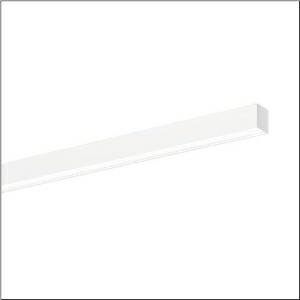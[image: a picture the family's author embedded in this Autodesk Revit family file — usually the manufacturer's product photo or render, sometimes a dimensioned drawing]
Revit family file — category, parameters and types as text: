
# Revit family: silica_21_51mx23dc3awb
name_source: partatom
category: Lighting Fixtures
units: mm (PartAtom-declared; Revit-internal decimal feet)

## family parameters
Cut with Voids When Loaded = No
Host = Face
Light Source = No
Part Type = Normal
Room Calculation Point = No
Round Connector Dimension = Use Diameter
Shared = No

## types (1)
- --- (1 x LED, 8200 lm, 62.2 W, 3000K)
    Apparent Load = 62 VA
    CIE Flux Codes = 78 96 99 100 100
    Color Rendering = 80
    Color Temperature = 3000K
    Default Elevation = 1800 mm
    Description = Silica 21, office luminaire, primary optical cover: prismatic diffuser, of PMMA, CAT 2 (L<= 3000cd/m²), light emission: direct distribution, primary light characteristic: symmetric, installation type: surface-mounted, LED, rated luminous flux: 8.200lm, luminous efficacy: 132lm/W, light colour: 830, colour temperature: 3000K, control gear: DALI 2, with terminal, 3+2-pole, max. 2.5mm², mains connection: 220..240V, AC, 50/60Hz, rated input power: 62.2W, luminaire housing, of aluminium, traffic white (RAL 9016), length: 3.004mm, width: 53mm, height: 53mm, protection rating (complete): IP20, insulation class (complete): insulation class I (protective earthing), certification: CE, permissible operating ambient temperature: 0..+35°C, standard: EN 50419, packaging unit: 1 piece
    Height = 53 mm
    Lamp = 1 x LED
    Lamp Light Flux = 8200 lm
    Lamp Power = 62.2 W
    Lamp count = 1
    Length = 3004 mm
    Luminous efficacy = 132 lm/W
    Manufacturer = Siteco
    ModVariant = No
    Model = 51MX23DC3AWB
    Mounting Place = Ceiling
    Mounting Type = Surface mounted
    Number of Poles = 1
    OnlyDefault = Yes
    Power Factor = 1
    Product Name = Silica 21
    Product group = office luminaire | ceiling mounted
    ProductGroupID = 301
    Protection Class = Protection class I
    Protection Degree = IP 20
    RLX_Detail_Level = 1
    RLX_Emergency_Light_Flux = 0 lm
    RLX_Emergency_Type = 0
    RLX_Emergency_Type_DB = No
    RlxData = <blob elided: 18741 chars, md5=76d5fc6f>
    Socket = socket
    Standby Power = 0 W
    System Light Flux = 8200 lm
    System Power = 62 W
    Type Comments = factory setting: luminous flux: 100 % | dim-lin: 254 | 345 mA
    Type Image = l_1335877.jpg
    URL = http://relux.com
    VarID = @adj_119631
    Voltage = 0 V
    Weight = 0.00 kg
    Width = 53 mm

## geometry (parser evidence)
native form markers: Blend x4, Sweep x11
no freeform markers — native parametric forms only
